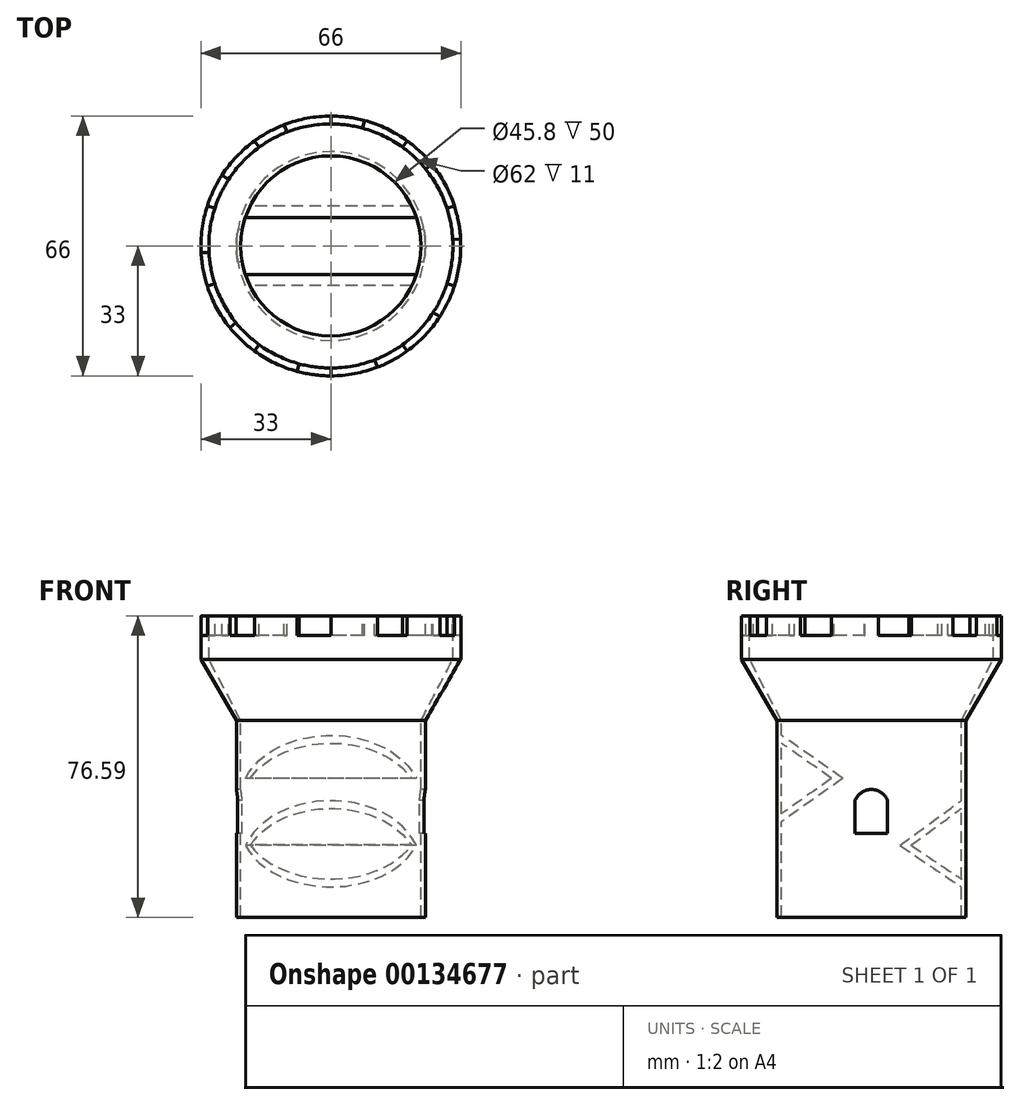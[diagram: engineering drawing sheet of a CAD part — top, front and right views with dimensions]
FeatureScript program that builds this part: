
annotation { "Feature Type Name" : "Feature", "Feature Type Description" : "" }
export const myFeature = defineFeature(function(context is Context, id is Id, definition is map)
    precondition{}
    {
        {
            var Q0;
            Q0=qCreatedBy(makeId("Top.planeOp"),FACE);
            var sketch = newSketch(context, id + "F0", { "sketchPlane" : qUnion([Q0])});
            skCircle(sketch, "E0", {"center": v(0, 0) * mm, "radius": 24 * mm});
            skSolve(sketch);
        }
        {
            var Q0;
            Q0=makeQuery(id+"F0.imprint","IMPRINT",FACE,{"disambiguationData":[TD([[makeQuery(id+"F0.imprint","IMPRINT",EDGE,{"derivedFrom":sQuery(id+"F0.wireOp",EDGE,"E0")}),1.0]])]});
            extrude(context, id + "F1", {"entities" : qUnion([Q0]), "depth" : 50 * mm});
        }
        {
            var Q0;
            Q0=makeQuery(id+"F1.opExtrude","CAP_FACE",FACE,{"disambiguationData":[OSD([sQuery(id+"F0.wireOp",EDGE,"E0")])],"isStart":false});
            var sketch = newSketch(context, id + "F2", { "sketchPlane" : qUnion([Q0])});
            skCircle(sketch, "E1", {"center": v(0, 0) * mm, "radius": 22.9 * mm});
            skSolve(sketch);
        }
        {
            var Q0;
            Q0=qSketchRegion(id+"F2",true);
            extrude(context, id + "F3", {"entities" : qUnion([Q0]), "operationType" : NewBodyOperationType.REMOVE, "endBound" : BoundingType.THROUGH_ALL, "oppositeDirection" : true, "depth" : 25 * mm});
        }
        {
            var Q0;
            Q0=qCreatedBy(makeId("Front.planeOp"),FACE);
            var sketch = newSketch(context, id + "F4", { "sketchPlane" : qUnion([Q0])});
            skLineSegment(sketch, "E2.0", {"start": v(-22.9, 50) * mm, "end": v(22.9, 50) * mm, "construction": true});
            skLineSegment(sketch, "E3.0", {"start": v(-24, 50) * mm, "end": v(24, 50) * mm, "construction": true});
            skLineSegment(sketch, "E4", {"start": v(0, 50) * mm, "end": v(0, 80) * mm, "construction": true});
            skPoint(sketch, "E4.endSnap0", {"position": v(0, 50) * mm});
            skLineSegment(sketch, "E5", {"start": v(-31, 76.59) * mm, "end": v(-33, 76.59) * mm});
            skLineSegment(sketch, "E6", {"start": v(-33, 76.59) * mm, "end": v(-33, 65.59) * mm});
            skLineSegment(sketch, "E7", {"start": v(-33, 65.59) * mm, "end": v(-24, 50) * mm});
            skLineSegment(sketch, "E8", {"start": v(-24, 50) * mm, "end": v(-22.9, 50) * mm});
            skLineSegment(sketch, "E9", {"start": v(-22.9, 50) * mm, "end": v(-31, 65.59) * mm});
            skLineSegment(sketch, "E10", {"start": v(-31, 65.59) * mm, "end": v(-31, 76.59) * mm});
            skLineSegment(sketch, "E11", {"start": v(-33, 65.59) * mm, "end": v(-33, 50) * mm, "construction": true});
            skSolve(sketch);
        }
        {
            var Q0;
            Q0=qSketchRegion(id+"F4",true);
            var Q1;
            Q1=makeQuery(id+"F3.boolean.opBoolean","COPY",FACE,{"derivedFrom":makeQuery(id+"F3.opExtrude","SWEPT_FACE",FACE,{"disambiguationData":[OSD([sQuery(id+"F2.wireOp",EDGE,"E1")])]})});
            revolve(context, id + "F5", {"operationType" : NewBodyOperationType.ADD, "entities" : qUnion([Q0]), "axis" : qUnion([Q1]), "revolveType" : RevolveType.FULL});
        }
        {
            var Q0;
            Q0=qCreatedBy(makeId("Right.planeOp"),FACE);
            var sketch = newSketch(context, id + "F6", { "sketchPlane" : qUnion([Q0])});
            skCircle(sketch, "E12", {"center": v(0, 27.55) * mm, "radius": 3 * mm});
            skLineSegment(sketch, "E13.rect.bottom", {"start": v(-3, 21.55) * mm, "end": v(3, 21.55) * mm});
            skLineSegment(sketch, "E13.rect.top", {"start": v(-3, 27.55) * mm, "end": v(3, 27.55) * mm});
            skLineSegment(sketch, "E13.rect.left", {"start": v(-3, 21.55) * mm, "end": v(-3, 27.55) * mm});
            skLineSegment(sketch, "E13.rect.right", {"start": v(3, 21.55) * mm, "end": v(3, 27.55) * mm});
            skPoint(sketch, "E13.rect.middle", {"position": v(0, 24.55) * mm});
            skSolve(sketch);
        }
        {
            var Q0;
            Q0=qCreatedBy(makeId("Right.planeOp"),FACE);
            var sketch = newSketch(context, id + "F7", { "sketchPlane" : qUnion([Q0])});
            skLineSegment(sketch, "E14", {"start": v(-22.9, 46.31) * mm, "end": v(-7.25, 35.31) * mm});
            skLineSegment(sketch, "E15", {"start": v(-7.25, 35.31) * mm, "end": v(-22.9, 24.31) * mm});
            skLineSegment(sketch, "E16", {"start": v(22.9, 7.71) * mm, "end": v(7.25, 18.3) * mm});
            skLineSegment(sketch, "E17", {"start": v(7.25, 18.3) * mm, "end": v(22.9, 29.71) * mm});
            skLineSegment(sketch, "E18", {"start": v(-22.9, 46.31) * mm, "end": v(-22.9, 44.31) * mm});
            skLineSegment(sketch, "E19", {"start": v(0, 18.3) * mm, "end": v(0, 35.31) * mm, "construction": true});
            skLineSegment(sketch, "E20", {"start": v(-7.25, 35.31) * mm, "end": v(0, 35.31) * mm, "construction": true});
            skLineSegment(sketch, "E21", {"start": v(0, 18.3) * mm, "end": v(7.25, 18.3) * mm, "construction": true});
            skLineSegment(sketch, "E22", {"start": v(-22.9, 24.31) * mm, "end": v(0, 24.31) * mm, "construction": true});
            skLineSegment(sketch, "E23", {"start": v(22.9, 29.71) * mm, "end": v(0, 29.71) * mm, "construction": true});
            skLineSegment(sketch, "E24", {"start": v(0, 29.71) * mm, "end": v(0, 24.31) * mm, "construction": true});
            skLineSegment(sketch, "E25", {"start": v(-22.9, 46.31) * mm, "end": v(-22.9, 24.31) * mm, "construction": true});
            skLineSegment(sketch, "E26", {"start": v(22.9, 29.71) * mm, "end": v(22.9, 7.71) * mm, "construction": true});
            skLineSegment(sketch, "E27.MirrorCS", {"start": v(-22.9, 24.31) * mm, "end": v(-22.9, 26.31) * mm});
            skLineSegment(sketch, "E28", {"start": v(-22.9, 44.31) * mm, "end": v(-10.1, 35.31) * mm});
            skLineSegment(sketch, "E29", {"start": v(-22.9, 26.31) * mm, "end": v(-10.1, 35.31) * mm});
            skLineSegment(sketch, "E30", {"start": v(22.9, 29.71) * mm, "end": v(22.9, 27.71) * mm});
            skLineSegment(sketch, "E31", {"start": v(22.9, 7.71) * mm, "end": v(22.9, 9.71) * mm});
            skLineSegment(sketch, "E32", {"start": v(22.9, 27.71) * mm, "end": v(10.1, 18.37) * mm});
            skLineSegment(sketch, "E33", {"start": v(22.9, 9.71) * mm, "end": v(10.1, 18.37) * mm});
            skLineSegment(sketch, "E34", {"start": v(-24, 0) * mm, "end": v(-24, 50) * mm, "construction": true});
            skLineSegment(sketch, "E35", {"start": v(22.9, 50) * mm, "end": v(22.9, 0) * mm, "construction": true});
            skLineSegment(sketch, "E36", {"start": v(-22.9, 0) * mm, "end": v(-22.9, 50) * mm, "construction": true});
            skSolve(sketch);
        }
        {
            var Q0;
            Q0=makeQuery(id+"F7.imprint","IMPRINT",FACE,{"disambiguationData":[TD([[makeQuery(id+"F7.imprint","IMPRINT",EDGE,{"derivedFrom":sQuery(id+"F7.wireOp",EDGE,"E14")}),-1.0]])]});
            var Q1;
            Q1=makeQuery(id+"F7.imprint","IMPRINT",FACE,{"disambiguationData":[TD([[makeQuery(id+"F7.imprint","IMPRINT",EDGE,{"derivedFrom":sQuery(id+"F7.wireOp",EDGE,"E16")}),-1.0]])]});
            var Q2;
            Q2=makeQuery(id+"F3.boolean.opBoolean","COPY",FACE,{"derivedFrom":makeQuery(id+"F3.opExtrude","SWEPT_FACE",FACE,{"disambiguationData":[OSD([sQuery(id+"F2.wireOp",EDGE,"E1")])]})});
            extrude(context, id + "F8", {"entities" : qUnion([Q0, Q1]), "operationType" : NewBodyOperationType.ADD, "endBound" : BoundingType.UP_TO_NEXT, "endBoundEntityFace" : qUnion([Q2]), "depth" : 25 * mm, "hasSecondDirection" : true, "secondDirectionBound" : SecondDirectionBoundingType.UP_TO_NEXT, "secondDirectionOppositeDirection" : true, "secondDirectionDepth" : 25 * mm, "offsetDistance" : 25 * mm});
        }
        {
            var Q0;
            Q0=makeQuery(id+"F5.opRevolve","SWEPT_FACE",FACE,{"disambiguationData":[OSD([sQuery(id+"F4.wireOp",EDGE,"E5")])]});
            var sketch = newSketch(context, id + "F9", { "sketchPlane" : qUnion([Q0])});
            skLineSegment(sketch, "E37", {"start": v(0, 0) * mm, "end": v(0, 33) * mm, "construction": true});
            skArc(sketch, "E38", {"start": v(8.54, 31.88) * mm, "mid": v(4.3, 32.72) * mm, "end": v(0, 33) * mm});
            skArc(sketch, "E39", {"start": v(8.02, 29.94) * mm, "mid": v(4.05, 30.73) * mm, "end": v(0, 31) * mm});
            skLineSegment(sketch, "E40", {"start": v(0, 33) * mm, "end": v(0, 31) * mm});
            skLineSegment(sketch, "E41", {"start": v(8.54, 31.88) * mm, "end": v(0, 0) * mm, "construction": true});
            skLineSegment(sketch, "E42", {"start": v(8.54, 31.88) * mm, "end": v(8.02, 29.94) * mm});
            skArc(sketch, "E43.1.0", {"start": v(-11.83, 30.8) * mm, "mid": v(-15.75, 29) * mm, "end": v(-19.4, 26.7) * mm});
            skArc(sketch, "E43.1.1", {"start": v(-11.1, 28.94) * mm, "mid": v(-14.8, 27.24) * mm, "end": v(-18.22, 25.08) * mm});
            skLineSegment(sketch, "E43.1.2", {"start": v(-11.83, 30.8) * mm, "end": v(-11.1, 28.94) * mm});
            skLineSegment(sketch, "E43.1.3", {"start": v(-19.4, 26.7) * mm, "end": v(-18.22, 25.08) * mm});
            skArc(sketch, "E43.2.0", {"start": v(-27.68, 17.97) * mm, "mid": v(-29.79, 14.2) * mm, "end": v(-31.38, 10.2) * mm});
            skArc(sketch, "E43.2.1", {"start": v(-26, 16.88) * mm, "mid": v(-27.98, 13.35) * mm, "end": v(-29.48, 9.58) * mm});
            skLineSegment(sketch, "E43.2.2", {"start": v(-27.68, 17.97) * mm, "end": v(-26, 16.88) * mm});
            skLineSegment(sketch, "E43.2.3", {"start": v(-31.38, 10.2) * mm, "end": v(-29.48, 9.58) * mm});
            skArc(sketch, "E44.3.3.0", {"start": v(-32.95, -1.73) * mm, "mid": v(-32.45, -6.01) * mm, "end": v(-31.38, -10.2) * mm});
            skArc(sketch, "E44.4.3.0", {"start": v(-30.96, -1.62) * mm, "mid": v(-30.48, -5.65) * mm, "end": v(-29.48, -9.58) * mm});
            skLineSegment(sketch, "E44.8.3.0", {"start": v(-32.95, -1.73) * mm, "end": v(-30.96, -1.62) * mm});
            skLineSegment(sketch, "E44.11.3.0", {"start": v(-31.38, -10.2) * mm, "end": v(-29.48, -9.58) * mm});
            skArc(sketch, "E44.3.4.0", {"start": v(-25.65, -20.77) * mm, "mid": v(-22.72, -23.94) * mm, "end": v(-19.4, -26.7) * mm});
            skArc(sketch, "E44.4.4.0", {"start": v(-24.1, -19.5) * mm, "mid": v(-21.34, -22.49) * mm, "end": v(-18.22, -25.08) * mm});
            skLineSegment(sketch, "E44.8.4.0", {"start": v(-25.65, -20.77) * mm, "end": v(-24.1, -19.5) * mm});
            skLineSegment(sketch, "E44.11.4.0", {"start": v(-19.4, -26.7) * mm, "end": v(-18.22, -25.08) * mm});
            skArc(sketch, "E45.3.5.0", {"start": v(-8.54, -31.88) * mm, "mid": v(-4.3, -32.72) * mm, "end": v(0, -33) * mm});
            skArc(sketch, "E45.4.5.0", {"start": v(-8.02, -29.94) * mm, "mid": v(-4.05, -30.73) * mm, "end": v(0, -31) * mm});
            skLineSegment(sketch, "E45.8.5.0", {"start": v(-8.54, -31.88) * mm, "end": v(-8.02, -29.94) * mm});
            skLineSegment(sketch, "E45.11.5.0", {"start": v(0, -33) * mm, "end": v(0, -31) * mm});
            skArc(sketch, "E45.3.6.0", {"start": v(11.83, -30.8) * mm, "mid": v(15.75, -29) * mm, "end": v(19.4, -26.7) * mm});
            skArc(sketch, "E45.4.6.0", {"start": v(11.1, -28.94) * mm, "mid": v(14.8, -27.24) * mm, "end": v(18.22, -25.08) * mm});
            skLineSegment(sketch, "E45.8.6.0", {"start": v(11.83, -30.8) * mm, "end": v(11.1, -28.94) * mm});
            skLineSegment(sketch, "E45.11.6.0", {"start": v(19.4, -26.7) * mm, "end": v(18.22, -25.08) * mm});
            skArc(sketch, "E45.3.7.0", {"start": v(27.68, -17.97) * mm, "mid": v(29.79, -14.2) * mm, "end": v(31.38, -10.2) * mm});
            skArc(sketch, "E45.4.7.0", {"start": v(26, -16.88) * mm, "mid": v(27.98, -13.35) * mm, "end": v(29.48, -9.58) * mm});
            skLineSegment(sketch, "E45.8.7.0", {"start": v(27.68, -17.97) * mm, "end": v(26, -16.88) * mm});
            skLineSegment(sketch, "E45.11.7.0", {"start": v(31.38, -10.2) * mm, "end": v(29.48, -9.58) * mm});
            skArc(sketch, "E45.3.8.0", {"start": v(32.95, 1.73) * mm, "mid": v(32.45, 6.01) * mm, "end": v(31.38, 10.2) * mm});
            skArc(sketch, "E45.4.8.0", {"start": v(30.96, 1.62) * mm, "mid": v(30.48, 5.65) * mm, "end": v(29.48, 9.58) * mm});
            skLineSegment(sketch, "E45.8.8.0", {"start": v(32.95, 1.73) * mm, "end": v(30.96, 1.62) * mm});
            skLineSegment(sketch, "E45.11.8.0", {"start": v(31.38, 10.2) * mm, "end": v(29.48, 9.58) * mm});
            skArc(sketch, "E45.3.9.0", {"start": v(25.65, 20.77) * mm, "mid": v(22.72, 23.94) * mm, "end": v(19.4, 26.7) * mm});
            skArc(sketch, "E45.4.9.0", {"start": v(24.1, 19.5) * mm, "mid": v(21.34, 22.49) * mm, "end": v(18.22, 25.08) * mm});
            skLineSegment(sketch, "E45.8.9.0", {"start": v(25.65, 20.77) * mm, "end": v(24.1, 19.5) * mm});
            skLineSegment(sketch, "E45.11.9.0", {"start": v(19.4, 26.7) * mm, "end": v(18.22, 25.08) * mm});
            skSolve(sketch);
        }
        {
            var Q0;
            Q0 = qSketchRegion(id + "F9", true);
            extrude(context, id + "F10", {"entities" : qUnion([Q0]), "operationType" : NewBodyOperationType.REMOVE, "oppositeDirection" : true, "depth" : 5 * mm, "offsetDistance" : 25 * mm});
        }
        {
            var Q0;
            Q0=qCreatedBy(makeId("Right.planeOp"),FACE);
            var sketch = newSketch(context, id + "F11", { "sketchPlane" : qUnion([Q0])});
            skPoint(sketch, "E46.0", {"position": v(0, 29.71) * mm});
            skPoint(sketch, "E47.0", {"position": v(0, 24.31) * mm});
            skPoint(sketch, "E48.0", {"position": v(0, 18.3) * mm});
            skPoint(sketch, "E49.0", {"position": v(0, 35.31) * mm});
            skLineSegment(sketch, "E50", {"start": v(0, 35.31) * mm, "end": v(0, 29.71) * mm, "construction": true});
            skLineSegment(sketch, "E51", {"start": v(0, 18.3) * mm, "end": v(0, 24.31) * mm, "construction": true});
            skPoint(sketch, "E52", {"position": v(0, 32.51) * mm});
            skPoint(sketch, "E53", {"position": v(0, 21.3) * mm});
            skArc(sketch, "E54", {"start": v(4.13, 29.71) * mm, "mid": v(0, 32.51) * mm, "end": v(-4.13, 29.71) * mm});
            skLineSegment(sketch, "E55", {"start": v(-4.13, 29.71) * mm, "end": v(-4.13, 21.3) * mm});
            skLineSegment(sketch, "E56", {"start": v(-4.13, 21.3) * mm, "end": v(4.13, 21.3) * mm});
            skLineSegment(sketch, "E57", {"start": v(4.13, 21.3) * mm, "end": v(4.13, 29.71) * mm});
            skSolve(sketch);
        }
        {
            var Q0;
            Q0 = qSketchRegion(id + "F11", true);
            extrude(context, id + "F12", {"entities" : qUnion([Q0]), "operationType" : NewBodyOperationType.REMOVE, "endBound" : BoundingType.THROUGH_ALL, "depth" : 25 * mm, "offsetDistance" : 25 * mm, "hasSecondDirection" : true, "secondDirectionBound" : SecondDirectionBoundingType.THROUGH_ALL, "secondDirectionOppositeDirection" : true, "secondDirectionDepth" : 25 * mm});
        }
    });
